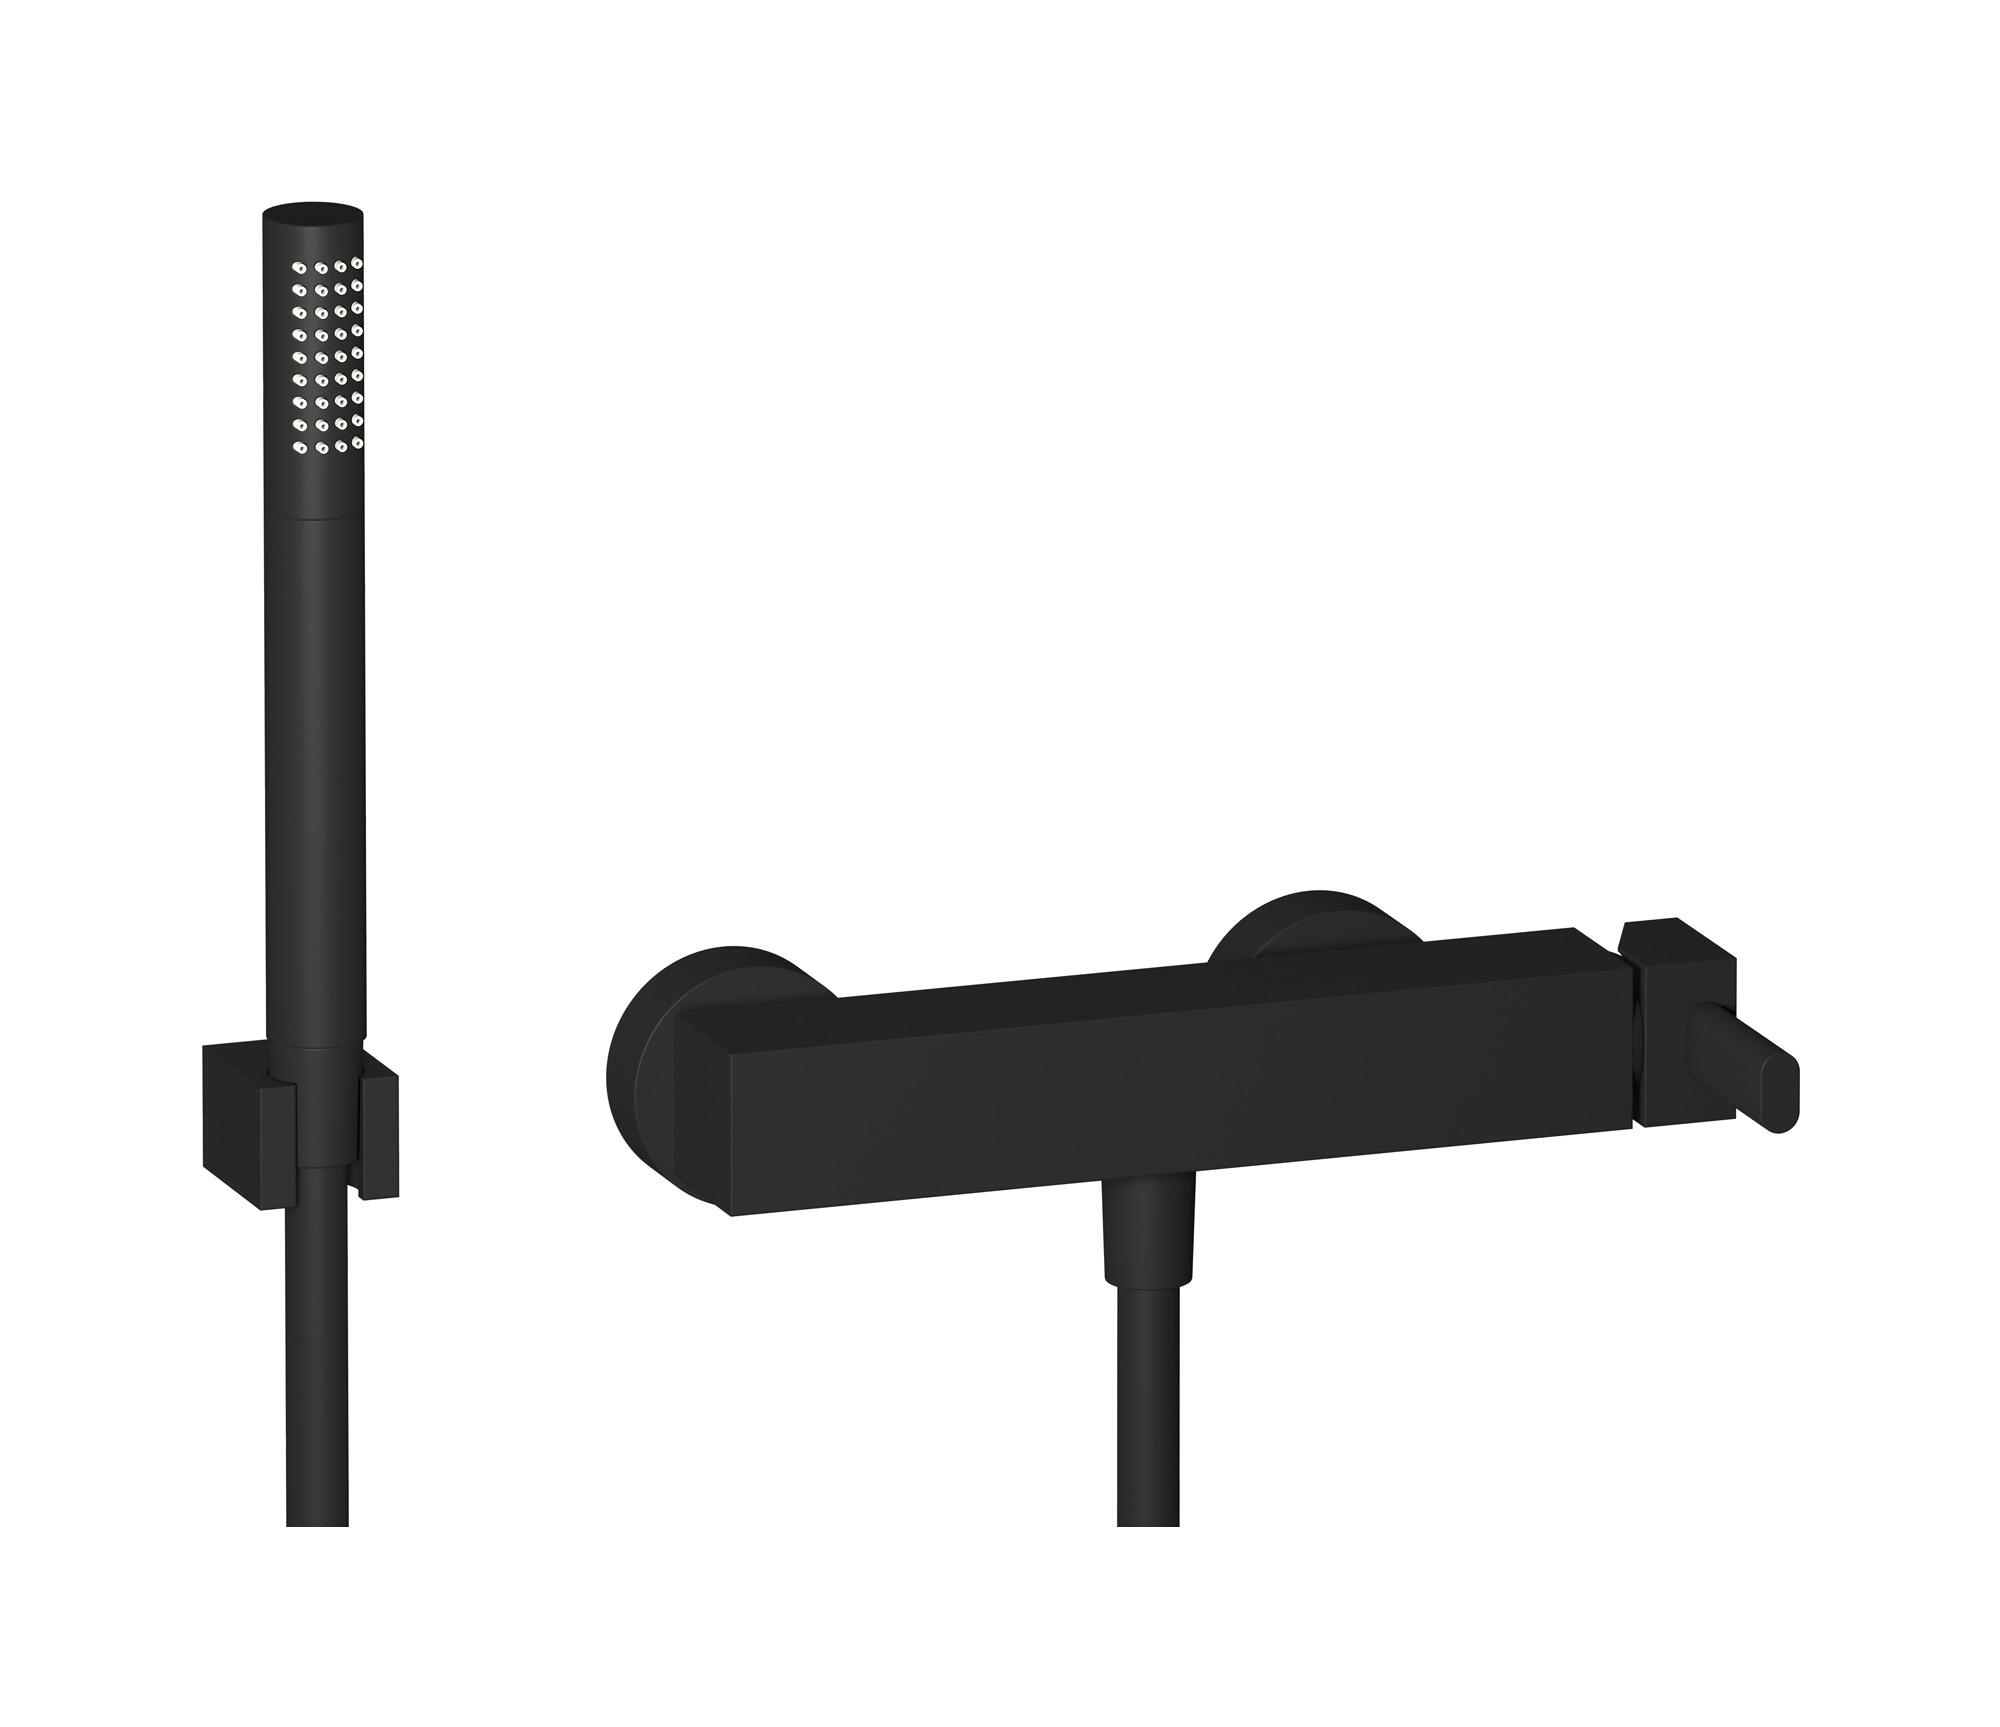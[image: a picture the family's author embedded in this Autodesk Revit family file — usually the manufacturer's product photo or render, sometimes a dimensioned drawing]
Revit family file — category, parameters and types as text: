
# Revit family: SB350
name_source: partatom
category: Apparecchi idraulici
units: mm (PartAtom-declared; Revit-internal decimal feet)

## family parameters
Basato su piano di lavoro = No
Condiviso = No
Mantieni orientamento annotazione = No
Numero OmniClass = 23.45.55.17
Punto di calcolo locali = No
Quota connettore circolare = Usa diametro
Sempre verticale = Sì
Taglio con vuoti quando caricato = No
Tipo di parte = Normale
Titolo OmniClass = Mixing Faucets

## types (6) — shared parameters
Cold water inlet = 10 mm  [stored 0.0328084 ft]
Commenti sul tipo = Shower mixer
Connessione CW = No
Connessione HW = No
Connessione di scarico = No
Connessione di ventilazione = No
Descrizione = Wall mounted shower mixer with shower kit
Hot water inlet = 10 mm  [stored 0.0328084 ft]
Produttore = IB Rubinetterie S.p.A.
URL = https://www.weareib.it
zero-valued in all types: Prospetto di default

## per-type parameters (varying)
| type | Finishes surface | Immagine tipo | Modello |
| Chrome | IB_Chrome | SB350CC.jpg | SB350CC |
| Brushed nickel | IB_Brushed nickel | SB350SS.jpg | SB350SS |
| Matt black | IB_matt black | SB350NP.jpg | SB350NP |
| Brushed gold | IB_brushed gold | SB350OS.jpg | SB350OS |
| Natural brass | IB_brushed gold | SB350ON.jpg | SB350ON |
| Rose gold | IB_Rose gold | SB350RS.jpg | SB350RS |

note: [stored X ft] marks values corroborated as IEEE doubles in the binary element streams (Revit-internal decimal feet)
